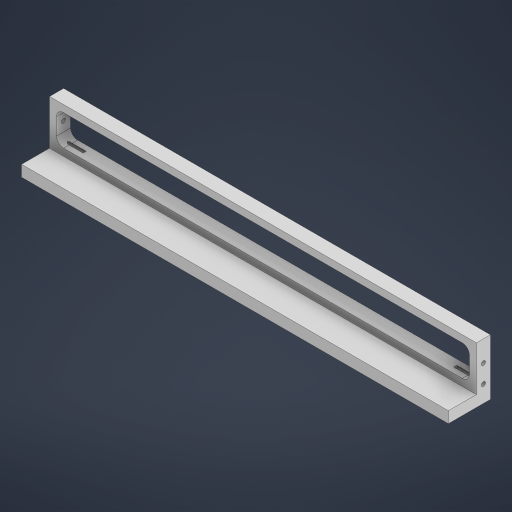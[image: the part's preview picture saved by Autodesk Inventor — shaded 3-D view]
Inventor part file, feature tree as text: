
AUTODESK INVENTOR PART (.ipt)
format: ipt  version: 2023 (Build 270158000, 158)  size: 257,536 bytes
history: native  units: mm
features: extrude x5, sketch x5, thread x4, fillet x1
ambient origin geometry x8: Origin, YZ Plane, XZ Plane, XY Plane, X Axis, Y Axis, Z Axis, Center Point
bodies: Solid1 (feature_tree)
feature tree (15):
  extrude  "Extrusion1"  Depth=10.0mm
  extrude  "Extrusion2"  Depth=8.0mm
  extrude  "Extrusion3"  Depth=5.0mm
  fillet  "Fillet2"  Radius=5.0mm
  extrude  "Extrusion4"  Depth=5.0mm TaperAngle=0.0deg
  extrude  "Extrusion5"  Depth=10.0mm
  thread  "Thread1"  [1 undecoded]
  thread  "Thread2"  [1 undecoded]
  thread  "Thread3"  [1 undecoded]
  thread  "Thread4"  [1 undecoded]
  sketch  "Sketch1"  dims[d0=305.0mm d1=10.0mm]
  sketch  "Sketch2"  dims[d2=40.0mm d3=0.0mm d4=8.0mm]
  sketch  "Sketch3"  dims[d5=20.0mm d6=0.0mm d8=5.0mm d9=5.0mm]
  sketch  "Sketch4"  dims[d10=5.0mm d11=20.0mm d12=0.0mm]
  sketch  "Sketch5"  dims[d13=5.0mm d14=3.0mm d15=3.0mm d16=15.0mm d17=10.0mm d18=5.0mm d19=5.0mm d20=20.0mm d21=0.0mm d22=3.0mm d23=3.0mm d24=5.0mm d25=5.0mm d26=10.0mm d27=15.0mm d28=20.0mm d29=0.0mm d30=5.23mm d31=0.0mm d32=5.67mm d33=0.0mm d34=5.23mm d35=0.0mm d36=5.67mm d37=0.0mm]
note: 4 required parameter values undecoded (feature->parameter linkage not recoverable at this tier; creation-order binding heuristic only, values carry confidence <= 0.55)
